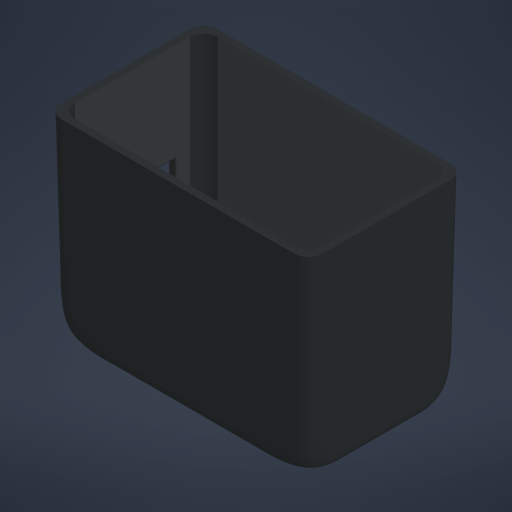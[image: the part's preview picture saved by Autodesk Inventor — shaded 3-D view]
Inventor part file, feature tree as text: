
AUTODESK INVENTOR PART (.ipt)
format: ipt  version: 2024 (Build 280153000, 153)  size: 614,400 bytes
history: native  units: in
note: dims shown in document units (in); Inventor stores cm internally (conversion verified against a paired STEP export)
features: chamfer x9, extrude x4, fillet x4, sketch x3, plane x2, boolean_combine x1
ambient origin geometry x8: Origin, YZ Plane, XZ Plane, XY Plane, X Axis, Y Axis, Z Axis, Center Point
bodies: Solid1 (feature_tree), Solid3 (feature_tree)
feature tree (23):
  extrude  "Extrusion1"  Depth=1.761in
  chamfer  "Chamfer1"  Distance=1.3in
  chamfer  "Chamfer3"  Distance=1.641in
  chamfer  "Chamfer4"  Distance=1.641in
  chamfer  "Chamfer5"  Distance=1.641in
  chamfer  "Chamfer6"  Distance=1.641in
  fillet  "Fillet2"  Radius=0.53in
  plane  "Work Plane8"
  extrude  "Extrusion8"  Depth=0.0625in
  boolean_combine  "Combine1"
  chamfer  "Chamfer8"  Distance=0.0625in
  chamfer  "Chamfer9"  Distance=0.0625in
  chamfer  "Chamfer10"  Distance=0.0625in
  chamfer  "Chamfer11"  Distance=0.0625in
  fillet  "Fillet3"  Radius=1.8045in
  plane  "Work Plane12"
  extrude  "Extrusion9"  Depth=1.8045in
  fillet  "Fillet4"  Radius=1.8045in
  fillet  "Fillet5"  Radius=1.8045in
  extrude  "Extrusion11"  Depth=1.8045in
  sketch  "Sketch11"  dims[d0=2.257in d1=1.761in d2=1.3in d3=0.0in]
  sketch  "Sketch16"  dims[d12=0.52in d30=0.12in d31=0.125in d32=0.2749in d36=1.641in d37=0.125in d38=0.0069in d39=1.641in d40=0.125in d41=0.0069in d42=1.641in d43=0.125in d44=0.0069in d45=1.641in d46=0.125in d47=0.0069in d48=0.53in d49=0.53in]
  sketch  "Sketch19"  dims[d78=1.0in d89=0.0625in d90=0.0625in d91=0.0625in d92=0.0625in d93=0.0625in d94=1.8045in d95=0.0in d99=1.8045in d100=0.125in d101=0.0069in d102=1.8045in d103=0.125in d104=0.0069in d105=1.8045in d106=0.125in d107=0.0069in d108=1.8045in d109=0.125in d110=0.0069in d111=0.5in d112=0.375in d113=0.5in d114=0.375in d115=0.5in d116=0.5in d117=0.375in d118=0.5in d119=0.5in d120=0.5in d121=0.375in d122=0.5in d123=0.125in d125=0.45in d127=0.135in d128=0.41in d129=0.509in d130=0.0in d131=0.0in d132=0.0156in d133=0.0104in d134=0.0625in d135=0.125in d148=0.0039in d149=0.0in d136=0.0in d137=0.0in]
